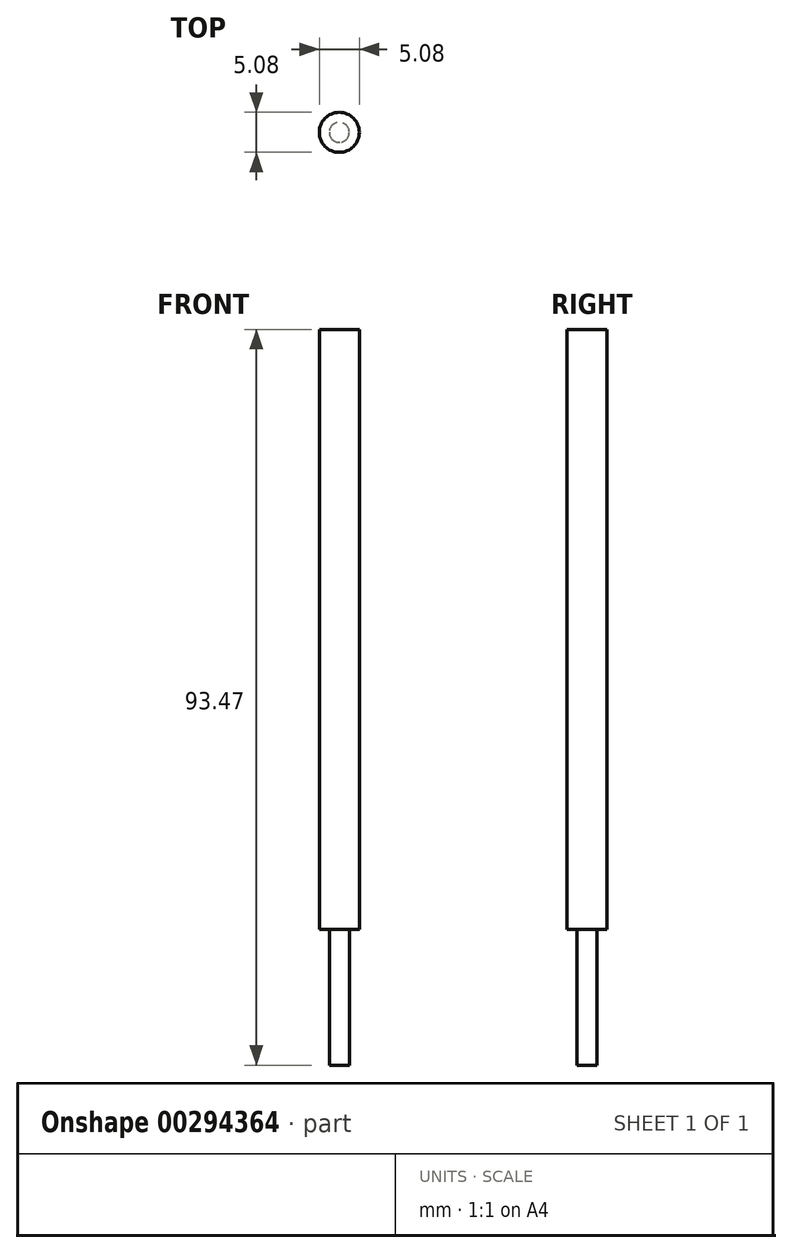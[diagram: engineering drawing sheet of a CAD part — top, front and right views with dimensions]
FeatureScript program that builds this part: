
annotation { "Feature Type Name" : "Feature", "Feature Type Description" : "" }
export const myFeature = defineFeature(function(context is Context, id is Id, definition is map)
    precondition{}
    {
        {
            var Q0;
            Q0=qCreatedBy(makeId("Top.planeOp"),FACE);
            var sketch = newSketch(context, id + "F0", { "sketchPlane" : qUnion([Q0])});
            skCircle(sketch, "E0", {"center": v(0, 0) * mm, "radius": 2.54 * mm});
            skSolve(sketch);
        }
        {
            var Q0;
            Q0 = qSketchRegion(id + "F0", true);
            extrude(context, id + "F1", {"entities" : qUnion([Q0]), "endBound" : BoundingType.SYMMETRIC, "depth" : 76.2 * mm});
        }
        {
            var Q0;
            Q0=makeQuery(id+"F1.opExtrude","CAP_FACE",FACE,{"disambiguationData":[OSD([sQuery(id+"F0.wireOp",EDGE,"E0")])],"isStart":true});
            var sketch = newSketch(context, id + "F2", { "sketchPlane" : qUnion([Q0])});
            skCircle(sketch, "E1", {"center": v(0, 0) * mm, "radius": 1.27 * mm});
            skSolve(sketch);
        }
        {
            var Q0;
            Q0 = qSketchRegion(id + "F2", true);
            extrude(context, id + "F3", {"entities" : qUnion([Q0]), "operationType" : NewBodyOperationType.ADD, "endBound" : BoundingType.SYMMETRIC, "depth" : 34.54 * mm});
        }
        {
            var Q0;
            Q0=qCreatedBy(makeId("Right.planeOp"),FACE);
            var sketch = newSketch(context, id + "F4", { "sketchPlane" : qUnion([Q0])});
            skLineSegment(sketch, "E2", {"start": v(1.18, -55.37) * mm, "end": v(2.8, -54.18) * mm});
            skLineSegment(sketch, "E3", {"start": v(1.27, -53.3) * mm, "end": v(2.8, -54.18) * mm});
            skSolve(sketch);
        }
        {
            var Q0;
            Q0 = qSketchRegion(id + "F4", true);
            var Q1;
            Q1 = qConstructionFilter(qBodyType(qCreatedBy(id + "F4" ,EDGE), BodyType.WIRE), ConstructionObject.NO);
            var Q2;
            Q2=makeQuery(id+"F3.opExtrude","SWEPT_FACE",FACE,{"disambiguationData":[OSD([sQuery(id+"F2.wireOp",EDGE,"E1")])]});
            revolve(context, id + "F5", {"bodyType" : ToolBodyType.SURFACE, "operationType" : NewBodyOperationType.ADD, "entities" : qUnion([Q0]), "surfaceEntities" : qUnion([Q1]), "axis" : qUnion([Q2]), "revolveType" : RevolveType.FULL});
        }
    });
